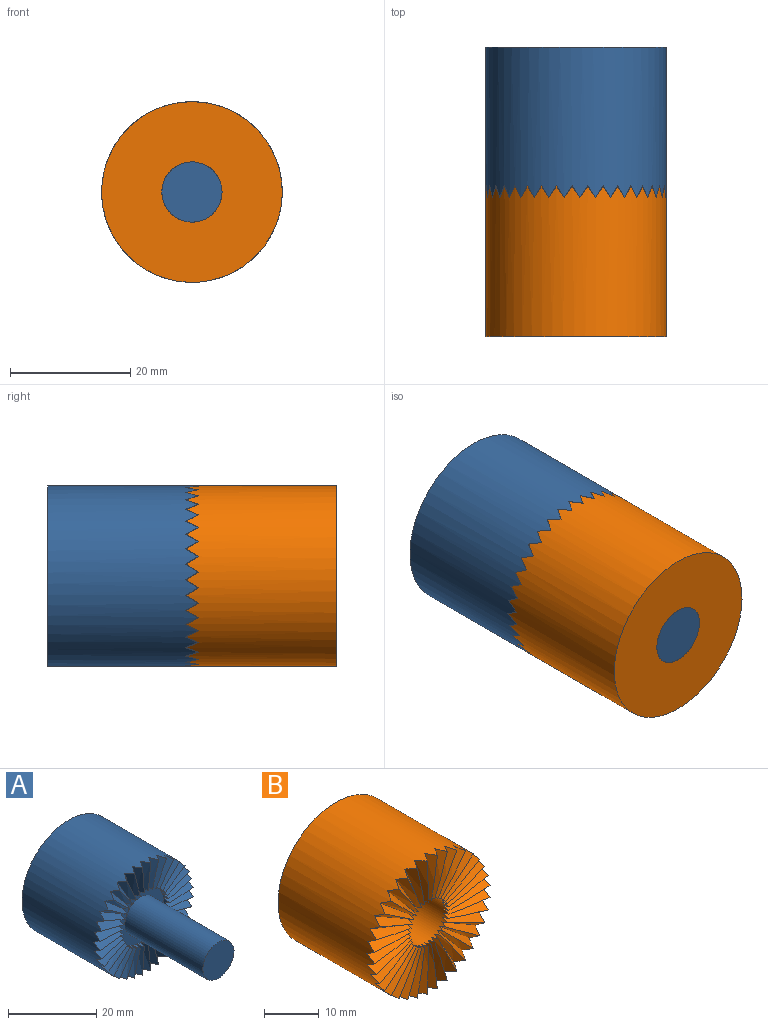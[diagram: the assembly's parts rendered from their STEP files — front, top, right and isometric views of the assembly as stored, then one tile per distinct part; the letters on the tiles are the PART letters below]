
ASSEMBLY  parts=2 mates=1
PART A: 113 faces, bbox 31x48x31 mm
  f0: cylinder r=7.5mm len=1.88mm, axis (0,-1,0), area 1.2mm2, adj f38,f40,f109
  f1: cylinder r=7.5mm len=1.88mm, axis (0,-1,0), area 1.2mm2, adj f38,f107,f110
  f2: cylinder r=7.5mm len=1.88mm, axis (0,-1,0), area 1.2mm2, adj f38,f105,f108
  f3: cylinder r=7.5mm len=1.88mm, axis (0,-1,0), area 1.2mm2, adj f38,f103,f106
  f4: cylinder r=7.5mm len=1.88mm, axis (0,-1,0), area 1.2mm2, adj f38,f101,f104
  f5: cylinder r=7.5mm len=1.88mm, axis (0,-1,0), area 1.2mm2, adj f38,f99,f102
  f6: cylinder r=7.5mm len=1.88mm, axis (0,-1,0), area 1.2mm2, adj f38,f97,f100
  f7: cylinder r=7.5mm len=1.88mm, axis (0,-1,0), area 1.2mm2, adj f38,f95,f98
  f8: cylinder r=7.5mm len=1.88mm, axis (0,-1,0), area 1.2mm2, adj f38,f93,f96
  f9: cylinder r=7.5mm len=1.88mm, axis (0,-1,0), area 1.2mm2, adj f38,f91,f94
  f10: cylinder r=7.5mm len=1.88mm, axis (0,-1,0), area 1.2mm2, adj f38,f89,f92
  f11: cylinder r=7.5mm len=1.88mm, axis (0,-1,0), area 1.2mm2, adj f38,f87,f90
  f12: cylinder r=7.5mm len=1.88mm, axis (0,-1,0), area 1.2mm2, adj f38,f85,f88
  f13: cylinder r=7.5mm len=1.88mm, axis (0,-1,0), area 1.2mm2, adj f38,f83,f86
  f14: cylinder r=7.5mm len=1.88mm, axis (0,-1,0), area 1.2mm2, adj f38,f81,f84
  f15: cylinder r=7.5mm len=1.88mm, axis (0,-1,0), area 1.2mm2, adj f38,f79,f82
  f16: cylinder r=7.5mm len=1.88mm, axis (0,-1,0), area 1.2mm2, adj f38,f77,f80
  f17: cylinder r=7.5mm len=1.88mm, axis (0,-1,0), area 1.2mm2, adj f38,f75,f78
  f18: cylinder r=7.5mm len=1.88mm, axis (0,-1,0), area 1.2mm2, adj f38,f73,f76
  f19: cylinder r=7.5mm len=1.88mm, axis (0,-1,0), area 1.2mm2, adj f38,f71,f74
  f20: cylinder r=7.5mm len=1.88mm, axis (0,-1,0), area 1.2mm2, adj f38,f69,f72
  f21: cylinder r=7.5mm len=1.88mm, axis (0,-1,0), area 1.2mm2, adj f38,f67,f70
  f22: cylinder r=7.5mm len=1.88mm, axis (0,-1,0), area 1.2mm2, adj f38,f65,f68
  f23: cylinder r=7.5mm len=1.88mm, axis (0,-1,0), area 1.2mm2, adj f38,f63,f66
  f24: cylinder r=7.5mm len=1.88mm, axis (0,-1,0), area 1.2mm2, adj f38,f61,f64
  f25: cylinder r=7.5mm len=1.88mm, axis (0,-1,0), area 1.2mm2, adj f38,f59,f62
  f26: cylinder r=7.5mm len=1.88mm, axis (0,-1,0), area 1.2mm2, adj f38,f57,f60
  f27: cylinder r=7.5mm len=1.88mm, axis (0,-1,0), area 1.2mm2, adj f38,f55,f58
  f28: cylinder r=7.5mm len=1.88mm, axis (0,-1,0), area 1.2mm2, adj f38,f53,f56
  f29: cylinder r=7.5mm len=1.88mm, axis (0,-1,0), area 1.2mm2, adj f38,f51,f54
  f30: cylinder r=7.5mm len=1.88mm, axis (0,-1,0), area 1.2mm2, adj f38,f49,f52
  f31: cylinder r=7.5mm len=1.88mm, axis (0,-1,0), area 1.2mm2, adj f38,f47,f50
  f32: cylinder r=7.5mm len=1.88mm, axis (0,-1,0), area 1.2mm2, adj f38,f45,f48
  f33: cylinder r=7.5mm len=1.88mm, axis (0,-1,0), area 1.2mm2, adj f38,f43,f46
  f34: cylinder r=7.5mm len=1.88mm, axis (0,-1,0), area 1.2mm2, adj f38,f41,f44
  f35: cylinder r=15mm len=30mm, axis (0,-1,0), area 2261.7mm2, adj f36,f39,f40,f41,f42,f43,f44,f45
  f36: plane 30x30mm, normal (0,1,0), area 706.9mm2, adj f35
  f37: cylinder r=7.5mm len=1.88mm, axis (0,-1,0), area 1.2mm2, adj f38,f39,f42
  f38: plane 15x15mm, normal (0,-1,0), area 98.2mm2, adj f0,f1,f2,f3,f4,f5,f6,f7
  f39: bspline ~8.5x2mm, area 16.3mm2, adj f35,f37,f40,f42
  f40: bspline ~8.5x2mm, area 16.3mm2, adj f0,f35,f39,f109
  f41: bspline ~8.49x2.81mm, area 16.3mm2, adj f34,f35,f42,f44
  f42: bspline ~8.61x2.12mm, area 16.3mm2, adj f35,f37,f39,f41
  f43: bspline ~8.21x4.18mm, area 16.3mm2, adj f33,f35,f44,f46
  f44: bspline ~8.45x3.52mm, area 16.3mm2, adj f34,f35,f41,f43
  f45: bspline ~7.69x5.42mm, area 16.3mm2, adj f32,f35,f46,f48
  f46: bspline ~8.04x4.82mm, area 16.3mm2, adj f33,f35,f43,f45
  f47: bspline ~6.93x6.5mm, area 16.3mm2, adj f31,f35,f48,f50
  f48: bspline ~7.38x5.97mm, area 16.3mm2, adj f32,f35,f45,f47
  f49: bspline ~7.38x5.97mm, area 16.3mm2, adj f30,f35,f50,f52
  f50: bspline ~6.93x6.5mm, area 16.3mm2, adj f31,f35,f47,f49
  f51: bspline ~8.04x4.82mm, area 16.3mm2, adj f29,f35,f52,f54
  f52: bspline ~7.69x5.42mm, area 16.3mm2, adj f30,f35,f49,f51
  f53: bspline ~8.45x3.52mm, area 16.3mm2, adj f28,f35,f54,f56
  f54: bspline ~8.21x4.18mm, area 16.3mm2, adj f29,f35,f51,f53
  f55: bspline ~8.61x2.12mm, area 16.3mm2, adj f27,f35,f56,f58
  f56: bspline ~8.49x2.81mm, area 16.3mm2, adj f28,f35,f53,f55
  f57: bspline ~8.5x2mm, area 16.3mm2, adj f26,f35,f58,f60
  f58: bspline ~8.5x2mm, area 16.3mm2, adj f27,f35,f55,f57
  f59: bspline ~8.49x2.81mm, area 16.3mm2, adj f25,f35,f60,f62
  f60: bspline ~8.61x2.12mm, area 16.3mm2, adj f26,f35,f57,f59
  f61: bspline ~8.21x4.18mm, area 16.3mm2, adj f24,f35,f62,f64
  f62: bspline ~8.45x3.52mm, area 16.3mm2, adj f25,f35,f59,f61
  f63: bspline ~7.69x5.42mm, area 16.3mm2, adj f23,f35,f64,f66
  f64: bspline ~8.04x4.82mm, area 16.3mm2, adj f24,f35,f61,f63
  f65: bspline ~6.93x6.5mm, area 16.3mm2, adj f22,f35,f66,f68
  f66: bspline ~7.38x5.97mm, area 16.3mm2, adj f23,f35,f63,f65
  f67: bspline ~7.38x5.97mm, area 16.3mm2, adj f21,f35,f68,f70
  f68: bspline ~6.93x6.5mm, area 16.3mm2, adj f22,f35,f65,f67
  f69: bspline ~8.04x4.82mm, area 16.3mm2, adj f20,f35,f70,f72
  f70: bspline ~7.69x5.42mm, area 16.3mm2, adj f21,f35,f67,f69
  f71: bspline ~8.45x3.52mm, area 16.3mm2, adj f19,f35,f72,f74
  f72: bspline ~8.21x4.18mm, area 16.3mm2, adj f20,f35,f69,f71
  f73: bspline ~8.61x2.12mm, area 16.3mm2, adj f18,f35,f74,f76
  f74: bspline ~8.49x2.81mm, area 16.3mm2, adj f19,f35,f71,f73
  f75: bspline ~8.5x2mm, area 16.3mm2, adj f17,f35,f76,f78
  f76: bspline ~8.5x2mm, area 16.3mm2, adj f18,f35,f73,f75
  f77: bspline ~8.49x2.81mm, area 16.3mm2, adj f16,f35,f78,f80
  f78: bspline ~8.61x2.12mm, area 16.3mm2, adj f17,f35,f75,f77
  f79: bspline ~8.21x4.18mm, area 16.3mm2, adj f15,f35,f80,f82
  f80: bspline ~8.45x3.52mm, area 16.3mm2, adj f16,f35,f77,f79
  f81: bspline ~7.69x5.42mm, area 16.3mm2, adj f14,f35,f82,f84
  f82: bspline ~8.04x4.82mm, area 16.3mm2, adj f15,f35,f79,f81
  f83: bspline ~6.93x6.5mm, area 16.3mm2, adj f13,f35,f84,f86
  f84: bspline ~7.38x5.97mm, area 16.3mm2, adj f14,f35,f81,f83
  f85: bspline ~7.38x5.97mm, area 16.3mm2, adj f12,f35,f86,f88
  f86: bspline ~6.93x6.5mm, area 16.3mm2, adj f13,f35,f83,f85
  f87: bspline ~8.04x4.82mm, area 16.3mm2, adj f11,f35,f88,f90
  f88: bspline ~7.69x5.42mm, area 16.3mm2, adj f12,f35,f85,f87
  f89: bspline ~8.45x3.52mm, area 16.3mm2, adj f10,f35,f90,f92
  f90: bspline ~8.21x4.18mm, area 16.3mm2, adj f11,f35,f87,f89
  f91: bspline ~8.61x2.12mm, area 16.3mm2, adj f9,f35,f92,f94
  f92: bspline ~8.49x2.81mm, area 16.3mm2, adj f10,f35,f89,f91
  f93: bspline ~8.5x2mm, area 16.3mm2, adj f8,f35,f94,f96
  f94: bspline ~8.5x2mm, area 16.3mm2, adj f9,f35,f91,f93
  f95: bspline ~8.49x2.81mm, area 16.3mm2, adj f7,f35,f96,f98
  f96: bspline ~8.61x2.12mm, area 16.3mm2, adj f8,f35,f93,f95
  f97: bspline ~8.21x4.18mm, area 16.3mm2, adj f6,f35,f98,f100
  f98: bspline ~8.45x3.52mm, area 16.3mm2, adj f7,f35,f95,f97
  f99: bspline ~7.69x5.42mm, area 16.3mm2, adj f5,f35,f100,f102
  f100: bspline ~8.04x4.82mm, area 16.3mm2, adj f6,f35,f97,f99
  f101: bspline ~6.93x6.5mm, area 16.3mm2, adj f4,f35,f102,f104
  f102: bspline ~7.38x5.97mm, area 16.3mm2, adj f5,f35,f99,f101
  f103: bspline ~7.38x5.97mm, area 16.3mm2, adj f3,f35,f104,f106
  f104: bspline ~6.93x6.5mm, area 16.3mm2, adj f4,f35,f101,f103
  f105: bspline ~8.04x4.82mm, area 16.3mm2, adj f2,f35,f106,f108
  f106: bspline ~7.69x5.42mm, area 16.3mm2, adj f3,f35,f103,f105
  f107: bspline ~8.45x3.52mm, area 16.3mm2, adj f1,f35,f108,f110
  f108: bspline ~8.21x4.18mm, area 16.3mm2, adj f2,f35,f105,f107
  f109: bspline ~8.61x2.12mm, area 16.3mm2, adj f0,f35,f40,f110
  f110: bspline ~8.49x2.81mm, area 16.3mm2, adj f1,f35,f107,f109
  f111: cylinder r=5mm len=25mm, axis (0,1,0), area 785.4mm2, adj f38,f112
  f112: plane 10x10mm, normal (0,-1,0), area 78.5mm2, adj f111
PART B: 75 faces, bbox 31x25x31 mm
  f0: cylinder r=15mm len=30mm, axis (0,-1,0), area 2261.1mm2, adj f1,f2,f3,f4,f5,f6,f7,f8
  f1: plane 30x30mm, normal (0,1,0), area 628.2mm2, adj f0,f74
  f2: bspline ~10.7x2mm, area 19.3mm2, adj f0,f3,f5,f74
  f3: bspline ~10.7x2mm, area 19.3mm2, adj f0,f2,f72,f74
  f4: bspline ~10.65x3.19mm, area 19.3mm2, adj f0,f5,f7,f74
  f5: bspline ~10.77x2.5mm, area 19.3mm2, adj f0,f2,f4,f74
  f6: bspline ~10.28x4.93mm, area 19.3mm2, adj f0,f7,f9,f74
  f7: bspline ~10.52x4.28mm, area 19.3mm2, adj f0,f4,f6,f74
  f8: bspline ~9.59x6.52mm, area 19.3mm2, adj f0,f9,f11,f74
  f9: bspline ~9.94x5.92mm, area 19.3mm2, adj f0,f6,f8,f74
  f10: bspline ~8.62x7.92mm, area 19.3mm2, adj f0,f11,f13,f74
  f11: bspline ~9.07x7.38mm, area 19.3mm2, adj f0,f8,f10,f74
  f12: bspline ~9.07x7.38mm, area 19.3mm2, adj f0,f13,f15,f74
  f13: bspline ~8.62x7.92mm, area 19.3mm2, adj f0,f10,f12,f74
  f14: bspline ~9.94x5.92mm, area 19.3mm2, adj f0,f15,f17,f74
  f15: bspline ~9.59x6.52mm, area 19.3mm2, adj f0,f12,f14,f74
  f16: bspline ~10.52x4.28mm, area 19.3mm2, adj f0,f17,f19,f74
  f17: bspline ~10.28x4.93mm, area 19.3mm2, adj f0,f14,f16,f74
  f18: bspline ~10.77x2.5mm, area 19.3mm2, adj f0,f19,f21,f74
  f19: bspline ~10.65x3.19mm, area 19.3mm2, adj f0,f16,f18,f74
  f20: bspline ~10.7x2mm, area 19.3mm2, adj f0,f21,f23,f74
  f21: bspline ~10.7x2mm, area 19.3mm2, adj f0,f18,f20,f74
  f22: bspline ~10.65x3.19mm, area 19.3mm2, adj f0,f23,f25,f74
  f23: bspline ~10.77x2.5mm, area 19.3mm2, adj f0,f20,f22,f74
  f24: bspline ~10.28x4.93mm, area 19.3mm2, adj f0,f25,f27,f74
  f25: bspline ~10.52x4.28mm, area 19.3mm2, adj f0,f22,f24,f74
  f26: bspline ~9.59x6.52mm, area 19.3mm2, adj f0,f27,f29,f74
  f27: bspline ~9.94x5.92mm, area 19.3mm2, adj f0,f24,f26,f74
  f28: bspline ~8.62x7.92mm, area 19.3mm2, adj f0,f29,f31,f74
  f29: bspline ~9.07x7.38mm, area 19.3mm2, adj f0,f26,f28,f74
  f30: bspline ~9.07x7.38mm, area 19.3mm2, adj f0,f31,f33,f74
  f31: bspline ~8.62x7.92mm, area 19.3mm2, adj f0,f28,f30,f74
  f32: bspline ~9.94x5.92mm, area 19.3mm2, adj f0,f33,f35,f74
  f33: bspline ~9.59x6.52mm, area 19.3mm2, adj f0,f30,f32,f74
  f34: bspline ~10.52x4.28mm, area 19.3mm2, adj f0,f35,f37,f74
  f35: bspline ~10.28x4.93mm, area 19.3mm2, adj f0,f32,f34,f74
  f36: bspline ~10.77x2.5mm, area 19.3mm2, adj f0,f37,f39,f74
  f37: bspline ~10.65x3.19mm, area 19.3mm2, adj f0,f34,f36,f74
  f38: bspline ~10.7x2mm, area 19.3mm2, adj f0,f39,f41,f74
  f39: bspline ~10.7x2mm, area 19.3mm2, adj f0,f36,f38,f74
  f40: bspline ~10.65x3.19mm, area 19.3mm2, adj f0,f41,f43,f74
  f41: bspline ~10.77x2.5mm, area 19.3mm2, adj f0,f38,f40,f74
  f42: bspline ~10.28x4.93mm, area 19.3mm2, adj f0,f43,f45,f74
  f43: bspline ~10.52x4.28mm, area 19.3mm2, adj f0,f40,f42,f74
  f44: bspline ~9.59x6.52mm, area 19.3mm2, adj f0,f45,f47,f74
  f45: bspline ~9.94x5.92mm, area 19.3mm2, adj f0,f42,f44,f74
  f46: bspline ~8.62x7.92mm, area 19.3mm2, adj f0,f47,f49,f74
  f47: bspline ~9.07x7.38mm, area 19.3mm2, adj f0,f44,f46,f74
  f48: bspline ~9.07x7.38mm, area 19.3mm2, adj f0,f49,f51,f74
  f49: bspline ~8.62x7.92mm, area 19.3mm2, adj f0,f46,f48,f74
  f50: bspline ~9.94x5.92mm, area 19.3mm2, adj f0,f51,f53,f74
  f51: bspline ~9.59x6.52mm, area 19.3mm2, adj f0,f48,f50,f74
  f52: bspline ~10.52x4.28mm, area 19.3mm2, adj f0,f53,f55,f74
  f53: bspline ~10.28x4.93mm, area 19.3mm2, adj f0,f50,f52,f74
  f54: bspline ~10.77x2.5mm, area 19.3mm2, adj f0,f55,f57,f74
  f55: bspline ~10.65x3.19mm, area 19.3mm2, adj f0,f52,f54,f74
  f56: bspline ~10.7x2mm, area 19.3mm2, adj f0,f57,f59,f74
  f57: bspline ~10.7x2mm, area 19.3mm2, adj f0,f54,f56,f74
  f58: bspline ~10.65x3.19mm, area 19.3mm2, adj f0,f59,f61,f74
  f59: bspline ~10.77x2.5mm, area 19.3mm2, adj f0,f56,f58,f74
  f60: bspline ~10.28x4.93mm, area 19.3mm2, adj f0,f61,f63,f74
  f61: bspline ~10.52x4.28mm, area 19.3mm2, adj f0,f58,f60,f74
  f62: bspline ~9.59x6.52mm, area 19.3mm2, adj f0,f63,f65,f74
  f63: bspline ~9.94x5.92mm, area 19.3mm2, adj f0,f60,f62,f74
  f64: bspline ~8.62x7.92mm, area 19.3mm2, adj f0,f65,f67,f74
  f65: bspline ~9.07x7.38mm, area 19.3mm2, adj f0,f62,f64,f74
  f66: bspline ~9.07x7.38mm, area 19.3mm2, adj f0,f67,f69,f74
  f67: bspline ~8.62x7.92mm, area 19.3mm2, adj f0,f64,f66,f74
  f68: bspline ~9.94x5.92mm, area 19.3mm2, adj f0,f69,f71,f74
  f69: bspline ~9.59x6.52mm, area 19.3mm2, adj f0,f66,f68,f74
  f70: bspline ~10.52x4.28mm, area 19.3mm2, adj f0,f71,f73,f74
  f71: bspline ~10.28x4.93mm, area 19.3mm2, adj f0,f68,f70,f74
  f72: bspline ~10.77x2.5mm, area 19.3mm2, adj f0,f3,f73,f74
  f73: bspline ~10.65x3.19mm, area 19.3mm2, adj f0,f70,f72,f74
  f74: cylinder r=5mm len=24.31mm, axis (0,-1,0), area 743.4mm2, adj f1,f2,f3,f4,f5,f6,f7,f8
PLACE A rot(axis=(0,1,0),7.5deg) t=(-2.17,-14.11,3.66)mm fixed
PLACE B rot(axis=(-0.02,0,-1),180deg) t=(-2.17,-12.11,3.66)mm
MATE fastened B.f74 <-> A.f111  axis (0,1,0) through (-2.17,-12.11,3.66)mm
